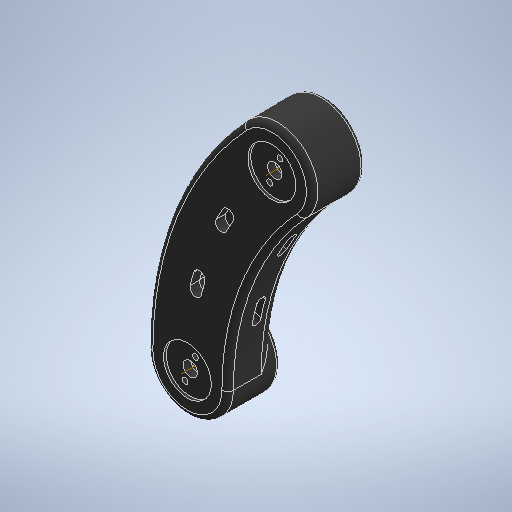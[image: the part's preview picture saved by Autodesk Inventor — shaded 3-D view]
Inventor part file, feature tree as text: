
AUTODESK INVENTOR PART (.ipt)
format: ipt  version: 2025.1 (Build 291241020, 241B)  size: 561,664 bytes
history: native  units: mm
features: sketch x9, extrude x8, projected_geometry x4, fillet x3, revolve x2, plane x2, other x2, shell x1, chamfer x1
ambient origin geometry x8: Origin, YZ Plane, XZ Plane, XY Plane, X Axis, Y Axis, Z Axis, Center Point
bodies: Solid1 (feature_tree)
feature tree (32):
  sketch  "Sketch2"  dims[d26=42.0mm d51=27.5mm d52=0.0mm d53=25.0mm d54=1.5mm d55=0.0mm]
  extrude  "Extrusion6"  Depth=27.5mm TaperAngle=0.0deg
  shell  "Shell1"  Thickness=25.0mm
  chamfer  "Chamfer1"  Distance=1.5mm
  extrude  "Extrusion9"  Depth=14.5mm
  extrude  "Extrusion1"  Depth=3.0mm
  extrude  "Extrusion2"  Depth=32.0mm
  extrude  "Extrusion3"  Depth=32.0mm
  extrude  "Extrusion4"  TaperAngle=90.0deg  [1 undecoded]
  revolve  "Revolution1"  [1 undecoded]
  plane  "Work Plane1"
  revolve  "Revolution2"  [1 undecoded]
  extrude  "Extrusion5"  Depth=13.75mm TaperAngle=0.0deg
  plane  "Work Plane2"
  extrude  "Extrusion10"  Depth=2.0mm TaperAngle=0.0deg
  fillet  "Fillet2"  Radius=5.0mm
  fillet  "Fillet3"  Radius=2.0mm
  fillet  "Fillet4"  Radius=6.0mm
  sketch  "Sketch3"  dims[d56=7.5mm d57=14.5mm]
  sketch  "Sketch4"  dims[d58=3.0mm d61=3.759439mm]
  sketch  "Sketch5"  dims[d62=1.5mm d63=0.0mm d64=32.0mm]
  sketch  "Sketch6"  dims[d65=1.0mm d66=0.0mm d67=32.0mm]
  sketch  "Sketch7"  dims[d70=13.0mm d71=90.0deg]
  projected_geometry  "Projected Loop1"
  projected_geometry  "Projected Loop2"
  sketch  "Sketch8"  dims[d73=22.0mm d74=0.0mm d106=3.759439mm]
  projected_geometry  "Projected Loop3"
  sketch  "Sketch13"  dims[d107=44.064mm d108=32.0mm d109=13.0mm]
  projected_geometry  "Projected Loop5"
  other  "Work Axis1"
  other  "Work Axis2"
  sketch  "Sketch14"  dims[d110=90.0deg d112=13.75mm d113=0.0mm d116=10.75mm d117=0.0mm d118=5.0mm d130=5.0mm d131=2.0mm d132=45.0deg d136=6.0mm d141=1.396263mm d142=0.0mm d143=0.0mm d144=0.436332mm d145=0.436332mm d146=239.999923mm d147=3.759971mm d149=10.0mm d151=40.0mm d152=60.0mm d153=0.0mm d154=0.0mm d155=7.0mm d156=3.0mm d157=2.0mm]
note: 3 required parameter values undecoded (feature->parameter linkage not recoverable at this tier; creation-order binding heuristic only, values carry confidence <= 0.55)